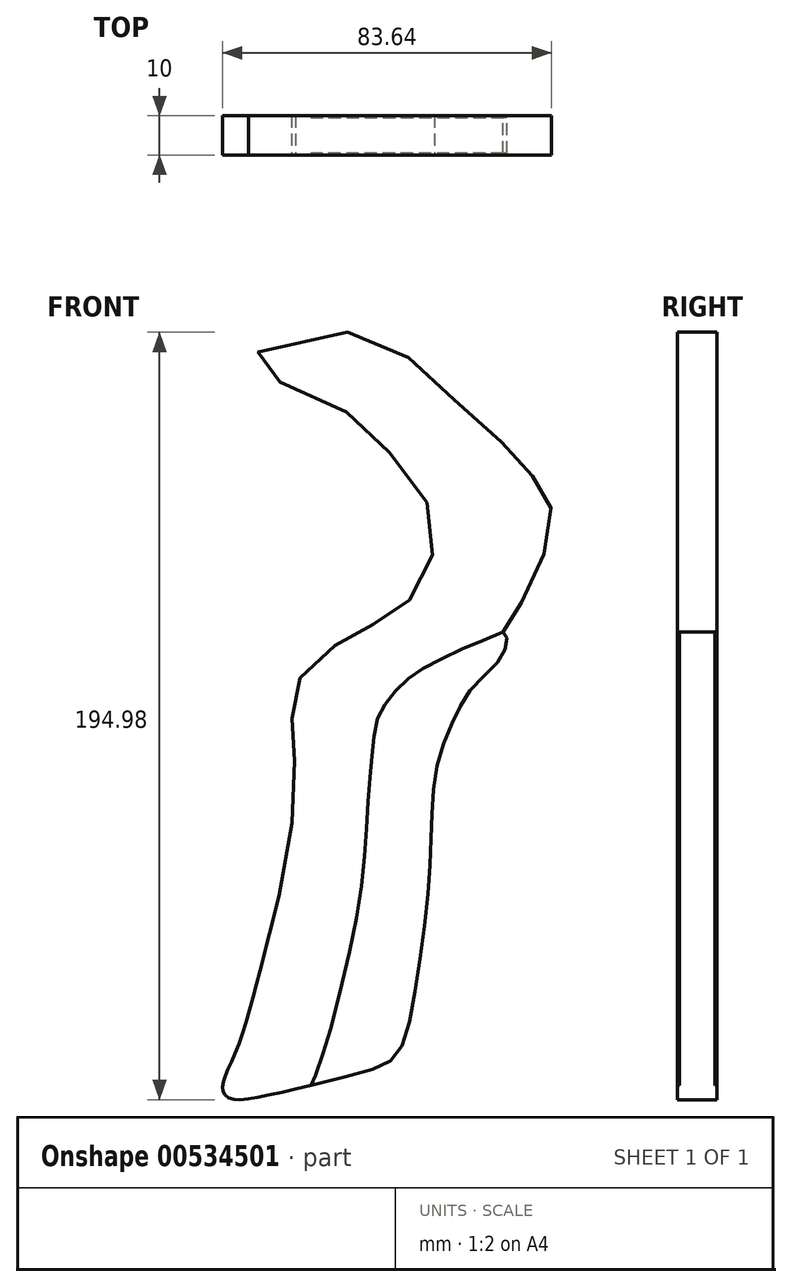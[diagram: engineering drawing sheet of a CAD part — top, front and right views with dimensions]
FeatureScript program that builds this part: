
annotation { "Feature Type Name" : "Feature", "Feature Type Description" : "" }
export const myFeature = defineFeature(function(context is Context, id is Id, definition is map)
    precondition{}
    {
        {
            var Q0;
            Q0=qCreatedBy(makeId("Front.planeOp"),FACE);
            var sketch = newSketch(context, id + "F0", { "sketchPlane" : qUnion([Q0])});
            skFitSpline(sketch, "E0", {"points": [v(-38.47, -27.8) * mm, v(-32.2, -2.04) * mm, v(-29.5, 21.26) * mm, v(-30.4, 31.34) * mm, v(-30.11, 39.26) * mm, v(-28.1, 46.87) * mm, v(-20.42, 54.24) * mm, v(-12.74, 58.6) * mm, v(-4.98, 63.1) * mm, v(1.83, 69.2) * mm, v(5.79, 81.8) * mm, v(2.15, 94.4) * mm, v(-10.29, 108.57) * mm, v(-23.6, 118.23) * mm, v(-41.38, 126.91) * mm, v(-13.11, 134.28) * mm, v(2.01, 125.17) * mm, v(16.24, 112.63) * mm, v(27.32, 101.86) * mm, v(31.92, 96.48) * mm, v(35.2, 90.99) * mm, v(34.92, 82.75) * mm, v(30.3, 70.02) * mm, v(25.47, 61.7) * mm, v(23.25, 58.22) * mm], "startDerivative": vector(136.57, 508.77) * mm, "endDerivative": vector(-102.14, -160.93) * mm});
            skFitSpline(sketch, "E1", {"points": [v(-38.47, -27.8) * mm, v(-44.28, -47.58) * mm, v(-47.6, -55.35) * mm, v(-47.83, -58.64) * mm, v(-45.82, -60.32) * mm, v(-37.08, -59.54) * mm, v(-11.43, -53.27) * mm, v(-3.37, -48.56) * mm, v(1.22, -31.1) * mm, v(4.37, -5.47) * mm, v(5.16, 11.48) * mm, v(6.75, 25.58) * mm, v(11.02, 36.66) * mm, v(15.34, 43.94) * mm, v(21.95, 50.61) * mm, v(24.06, 55.03) * mm, v(24.06, 57.38) * mm, v(23.25, 58.22) * mm], "startDerivative": vector(-66.86, -258.43) * mm, "endDerivative": vector(-37.66, 44.27) * mm});
            skFitSpline(sketch, "E2", {"points": [v(23.25, 58.22) * mm, v(13.87, 54.36) * mm, v(4.46, 49.85) * mm, v(-1.18, 46.12) * mm, v(-5.65, 41.32) * mm, v(-8.46, 36.77) * mm, v(-9.79, 29.8) * mm, v(-10.63, 20.57) * mm, v(-11.59, 6.46) * mm, v(-13.5, -12.02) * mm, v(-18.25, -33.63) * mm, v(-21.02, -44.24) * mm, v(-24.66, -55.09) * mm, v(-25.53, -56.94) * mm], "startDerivative": vector(-117.51, -46.8) * mm, "endDerivative": vector(-21.1, -38.72) * mm});
            skSolve(sketch);
        }
        {
            var Q0;
            Q0=makeQuery(id+"F0.imprint","IMPRINT",FACE,{"disambiguationData":[TD([[makeQuery(id+"F0.imprint","IMPRINT",EDGE,{"derivedFrom":sQuery(id+"F0.wireOp",EDGE,"E0")}),-1.0]])]});
            extrude(context, id + "F1", {"entities" : qUnion([Q0]), "endBound" : BoundingType.SYMMETRIC, "depth" : 10 * mm, "offsetDistance" : 25 * mm});
        }
        {
            var Q0;
            Q0=makeQuery(id+"F0.imprint","IMPRINT",FACE,{"disambiguationData":[TD([[makeQuery(id+"F0.imprint","IMPRINT",EDGE,{"derivedFrom":sQuery(id+"F0.wireOp",EDGE,"E2")}),1.0]])]});
            extrude(context, id + "F2", {"entities" : qUnion([Q0]), "operationType" : NewBodyOperationType.ADD, "endBound" : BoundingType.SYMMETRIC, "depth" : 9 * mm, "offsetDistance" : 25 * mm});
        }
    });
